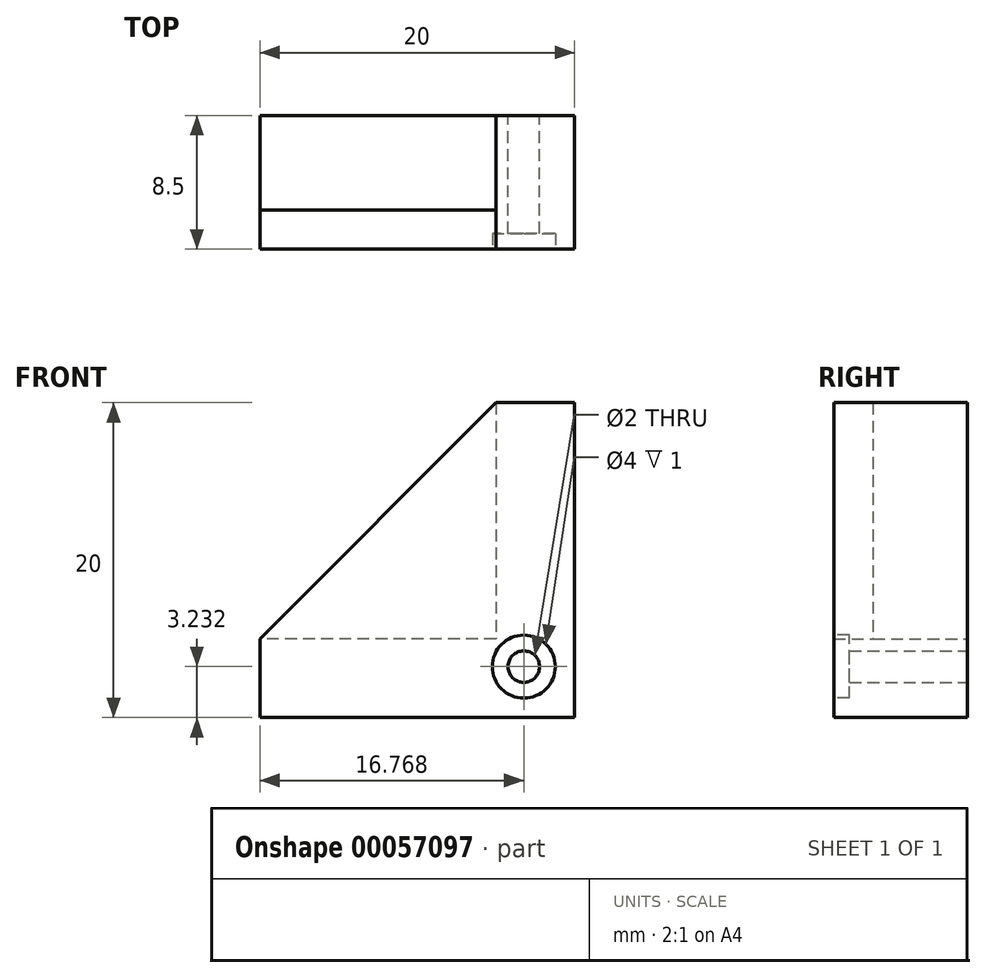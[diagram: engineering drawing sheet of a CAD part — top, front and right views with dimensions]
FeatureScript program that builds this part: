
annotation { "Feature Type Name" : "Feature", "Feature Type Description" : "" }
export const myFeature = defineFeature(function(context is Context, id is Id, definition is map)
    precondition{}
    {
        {
            var Q0;
            Q0=qCreatedBy(makeId("Front.planeOp"),FACE);
            var sketch = newSketch(context, id + "F0", { "sketchPlane" : qUnion([Q0])});
            skLineSegment(sketch, "E0.rect.bottom", {"start": v(3, 18) * mm, "end": v(-2, 18) * mm});
            skLineSegment(sketch, "E0.rect.left", {"start": v(3, 18) * mm, "end": v(3, -2) * mm});
            skLineSegment(sketch, "E0.rect.right", {"start": v(-2, 18) * mm, "end": v(-2, 3) * mm});
            skPoint(sketch, "E0.rect.middle", {"position": v(0, 0) * mm});
            skLineSegment(sketch, "E1.rect.right", {"start": v(-17, 3) * mm, "end": v(-17, -2) * mm});
            skLineSegment(sketch, "E2.trimOffspring", {"start": v(3, -2) * mm, "end": v(-17, -2) * mm});
            skLineSegment(sketch, "E3.trimOffspring", {"start": v(-2, 3) * mm, "end": v(-17, 3) * mm});
            skSolve(sketch);
        }
        {
            var Q0;
            Q0=qSketchRegion(id+"F0",true);
            extrude(context, id + "F1", {"entities" : qUnion([Q0]), "depth" : 6 * mm});
        }
        {
            var Q0;
            Q0=makeQuery(id+"F1.opExtrude","CAP_FACE",FACE,{"disambiguationData":[OSD([sQuery(id+"F0.wireOp",EDGE,"E0.rect.bottom"),sQuery(id+"F0.wireOp",EDGE,"E0.rect.top"),sQuery(id+"F0.wireOp",EDGE,"E0.rect.left"),sQuery(id+"F0.wireOp",EDGE,"E0.rect.right"),sQuery(id+"F0.wireOp",EDGE,"E1.rect.bottom"),sQuery(id+"F0.wireOp",EDGE,"E1.rect.top"),sQuery(id+"F0.wireOp",EDGE,"E1.rect.left"),sQuery(id+"F0.wireOp",EDGE,"E1.rect.right"),sQuery(id+"F0.wireOp",EDGE,"f1715e6e-c9c8-4c08-b6ac-1857fe2d7ea6.trimOffspring"),sQuery(id+"F0.wireOp",EDGE,"E2.trimOffspring"),sQuery(id+"F0.wireOp",EDGE,"66311b8e-0adb-4d38-ba11-cad6fc81466d.trimOffspring"),sQuery(id+"F0.wireOp",EDGE,"E3.trimOffspring")])],"isStart":false});
            var sketch = newSketch(context, id + "F2", { "sketchPlane" : qUnion([Q0])});
            skLineSegment(sketch, "E4", {"start": v(-17, 3) * mm, "end": v(-2, 18) * mm});
            skLineSegment(sketch, "E5.0", {"start": v(3, 18) * mm, "end": v(3, -2) * mm});
            skLineSegment(sketch, "E5.1", {"start": v(3, -2) * mm, "end": v(-17, -2) * mm});
            skPoint(sketch, "E6.orphan", {"position": v(-17, -3) * mm});
            skLineSegment(sketch, "E7", {"start": v(-17, 3) * mm, "end": v(-17, -2) * mm});
            skLineSegment(sketch, "E8", {"start": v(-2, 18) * mm, "end": v(3, 18) * mm});
            skSolve(sketch);
        }
        {
            var Q0;
            Q0=qSketchRegion(id+"F2",true);
            extrude(context, id + "F3", {"entities" : qUnion([Q0]), "operationType" : NewBodyOperationType.ADD, "depth" : 2.5 * mm});
        }
        {
            var Q0;
            Q0=makeQuery(id+"F1.opExtrude","CAP_FACE",FACE,{"disambiguationData":[OSD([sQuery(id+"F0.wireOp",EDGE,"E0.rect.bottom"),sQuery(id+"F0.wireOp",EDGE,"E0.rect.top"),sQuery(id+"F0.wireOp",EDGE,"E0.rect.left"),sQuery(id+"F0.wireOp",EDGE,"E0.rect.right"),sQuery(id+"F0.wireOp",EDGE,"E1.rect.bottom"),sQuery(id+"F0.wireOp",EDGE,"E1.rect.top"),sQuery(id+"F0.wireOp",EDGE,"E1.rect.left"),sQuery(id+"F0.wireOp",EDGE,"E1.rect.right"),sQuery(id+"F0.wireOp",EDGE,"f1715e6e-c9c8-4c08-b6ac-1857fe2d7ea6.trimOffspring"),sQuery(id+"F0.wireOp",EDGE,"E2.trimOffspring"),sQuery(id+"F0.wireOp",EDGE,"66311b8e-0adb-4d38-ba11-cad6fc81466d.trimOffspring"),sQuery(id+"F0.wireOp",EDGE,"E3.trimOffspring")])],"isStart":true});
            var sketch = newSketch(context, id + "F4", { "sketchPlane" : qUnion([Q0])});
            skLineSegment(sketch, "E9", {"start": v(-3, -2) * mm, "end": v(2, 3) * mm, "construction": true});
            skCircle(sketch, "E10", {"center": v(0.23, 1.23) * mm, "radius": 1 * mm});
            skSolve(sketch);
        }
        {
            var Q0;
            Q0=qSketchRegion(id+"F4",true);
            extrude(context, id + "F5", {"entities" : qUnion([Q0]), "operationType" : NewBodyOperationType.REMOVE, "endBound" : BoundingType.THROUGH_ALL, "oppositeDirection" : true, "depth" : 25 * mm});
        }
        {
            var Q0;
            Q0=makeQuery(id+"F3.opExtrude","CAP_FACE",FACE,{"disambiguationData":[OSD([sQuery(id+"F2.wireOp",EDGE,"E4"),sQuery(id+"F2.wireOp",EDGE,"QSpX1bc1-mrEP-ybLa-qeSf-WfqxeROanqX6"),sQuery(id+"F2.wireOp",EDGE,"MW7mzmCs-9JJE-a0P1-dliN-j179De4u7hKX"),sQuery(id+"F2.wireOp",EDGE,"84f4f8a6-141e-4e70-b4aa-45cea531d95f2.MirrorCS"),sQuery(id+"F2.wireOp",EDGE,"8fff74bd-808f-43f4-8d25-7f1f4a39cee23.MirrorCS"),sQuery(id+"F2.wireOp",EDGE,"E5.0"),sQuery(id+"F2.wireOp",EDGE,"E5.1")])],"isStart":false});
            var sketch = newSketch(context, id + "F6", { "sketchPlane" : qUnion([Q0])});
            skCircle(sketch, "E11", {"center": v(-0.23, 1.23) * mm, "radius": 2 * mm});
            skSolve(sketch);
        }
        {
            var Q0;
            Q0=makeQuery(id+"F6.imprint","IMPRINT",FACE,{"disambiguationData":[TD([[makeQuery(id+"F6.imprint","IMPRINT",EDGE,{"derivedFrom":sQuery(id+"F6.wireOp",EDGE,"E11")}),1.0]])]});
            extrude(context, id + "F7", {"entities" : qUnion([Q0]), "operationType" : NewBodyOperationType.REMOVE, "oppositeDirection" : true, "depth" : 1 * mm});
        }
    });
